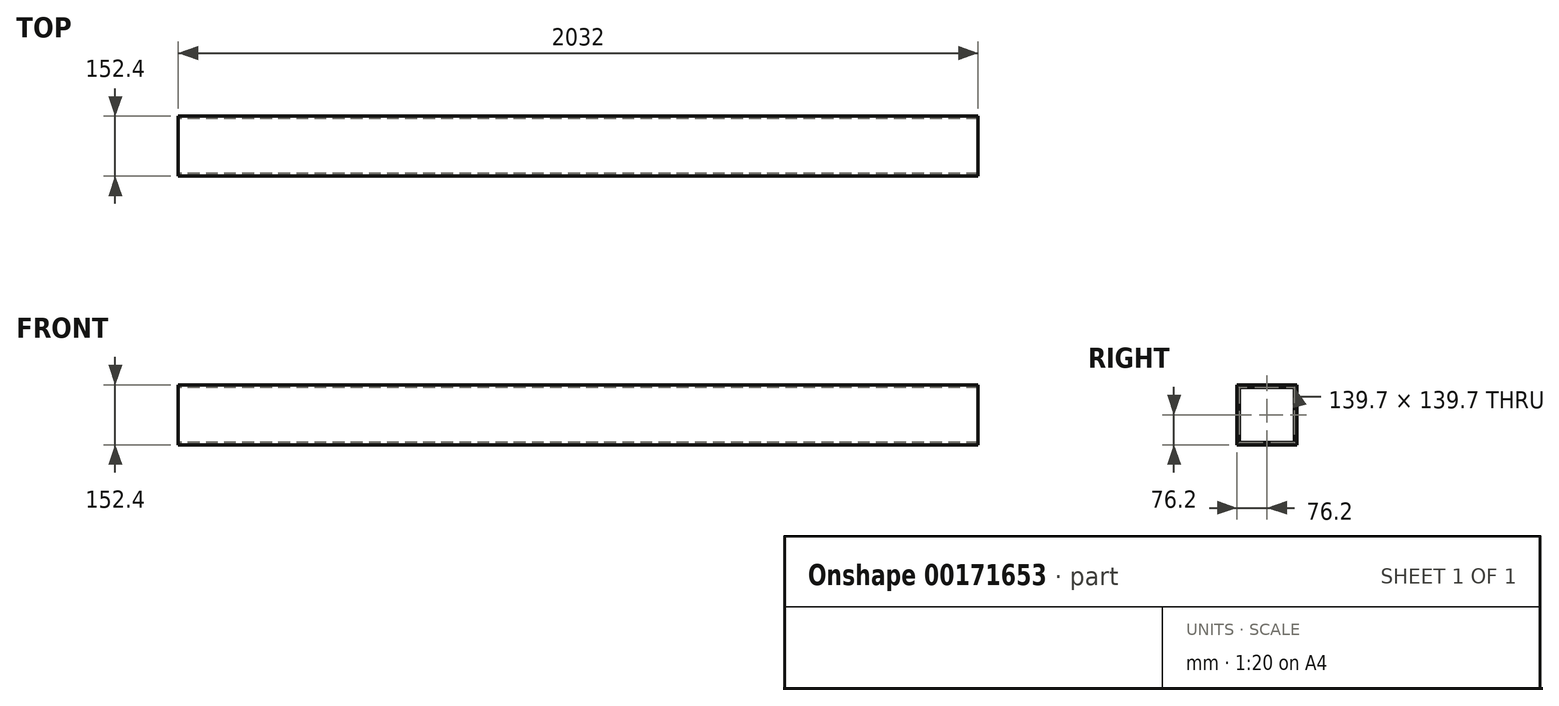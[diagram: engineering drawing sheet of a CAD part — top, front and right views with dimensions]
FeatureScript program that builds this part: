
annotation { "Feature Type Name" : "Feature", "Feature Type Description" : "" }
export const myFeature = defineFeature(function(context is Context, id is Id, definition is map)
    precondition{}
    {
        {
            var Q0;
            Q0=qCreatedBy(makeId("Right.planeOp"),FACE);
            var sketch = newSketch(context, id + "F0", { "sketchPlane" : qUnion([Q0])});
            skLineSegment(sketch, "E0.bottom", {"start": v(-76.2, 76.2) * mm, "end": v(76.2, 76.2) * mm});
            skLineSegment(sketch, "E0.top", {"start": v(-76.2, -76.2) * mm, "end": v(76.2, -76.2) * mm});
            skLineSegment(sketch, "E0.left", {"start": v(-76.2, 76.2) * mm, "end": v(-76.2, -76.2) * mm});
            skLineSegment(sketch, "E0.right", {"start": v(76.2, 76.2) * mm, "end": v(76.2, -76.2) * mm});
            skLineSegment(sketch, "E1.bottom", {"start": v(-69.85, 69.85) * mm, "end": v(69.85, 69.85) * mm});
            skLineSegment(sketch, "E1.top", {"start": v(-69.85, -69.85) * mm, "end": v(69.85, -69.85) * mm});
            skLineSegment(sketch, "E1.left", {"start": v(-69.85, 69.85) * mm, "end": v(-69.85, -69.85) * mm});
            skLineSegment(sketch, "E1.right", {"start": v(69.85, 69.85) * mm, "end": v(69.85, -69.85) * mm});
            skSolve(sketch);
        }
        {
            var Q0;
            Q0=makeQuery(id+"F0.imprint","IMPRINT",FACE,{"disambiguationData":[TD([[makeQuery(id+"F0.imprint","IMPRINT",EDGE,{"derivedFrom":sQuery(id+"F0.wireOp",EDGE,"E0.bottom")}),-1.0]])]});
            extrude(context, id + "F1", {"entities" : qUnion([Q0]), "depth" : 2032 * mm});
        }
    });
